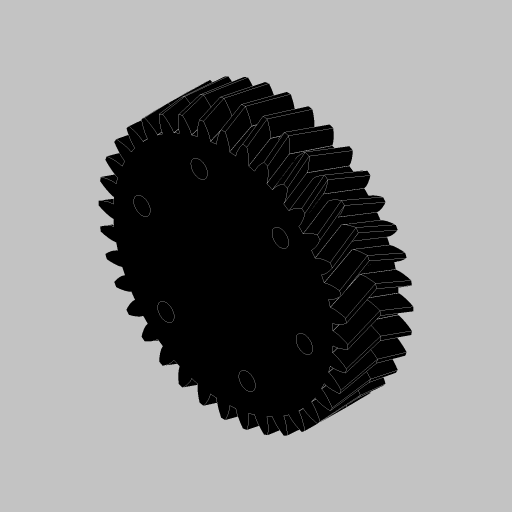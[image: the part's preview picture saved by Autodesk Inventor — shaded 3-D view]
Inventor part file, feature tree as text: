
AUTODESK INVENTOR PART (.ipt)
format: ipt  version: 2023.5 (Build 275446000, 446)  size: 1,206,272 bytes
history: native  units: in
note: dims shown in document units (in); Inventor stores cm internally (conversion verified against a paired STEP export)
features: hole x1, sketch x1, other x1, projected_geometry x1
ambient origin geometry x8: Origin, YZ Plane, XZ Plane, XY Plane, X Axis, Y Axis, Z Axis, Center Point
bodies: Solid1 (feature_tree)
feature tree (4):
  hole  "Hole1"  [1 undecoded]
  sketch  "Sketch1"  dims[d0=2.8148in d1=2.0in d2=2.3622in d4=360.0deg d6=0.201in d7=0.75in d8=0.385in d9=0.25in d10=0.5635in d11=1.0in d12=0.8108in]
  other  "Helical 2M 36T"
  projected_geometry  "Project Cut Edges1"
note: 1 required parameter value undecoded (feature->parameter linkage not recoverable at this tier; creation-order binding heuristic only, values carry confidence <= 0.55)
